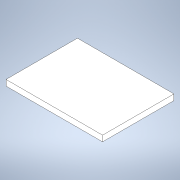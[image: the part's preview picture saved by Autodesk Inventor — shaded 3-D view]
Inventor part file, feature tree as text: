
AUTODESK INVENTOR PART (.ipt)
format: ipt  version: 2022 (Build 260153000, 153)  size: 90,112 bytes
history: native  units: in
note: dims shown in document units (in); Inventor stores cm internally (conversion verified against a paired STEP export)
features: extrude x1, sketch x1
ambient origin geometry x8: Origin, YZ Plane, XZ Plane, XY Plane, X Axis, Y Axis, Z Axis, Center Point
bodies: Solid1 (feature_tree)
feature tree (2):
  extrude  "Extrusion1"  Depth=7.2835in
  sketch  "Sketch1"  dims[d0=9.8425in d1=7.2835in d2=0.5906in d3=0.0in]
